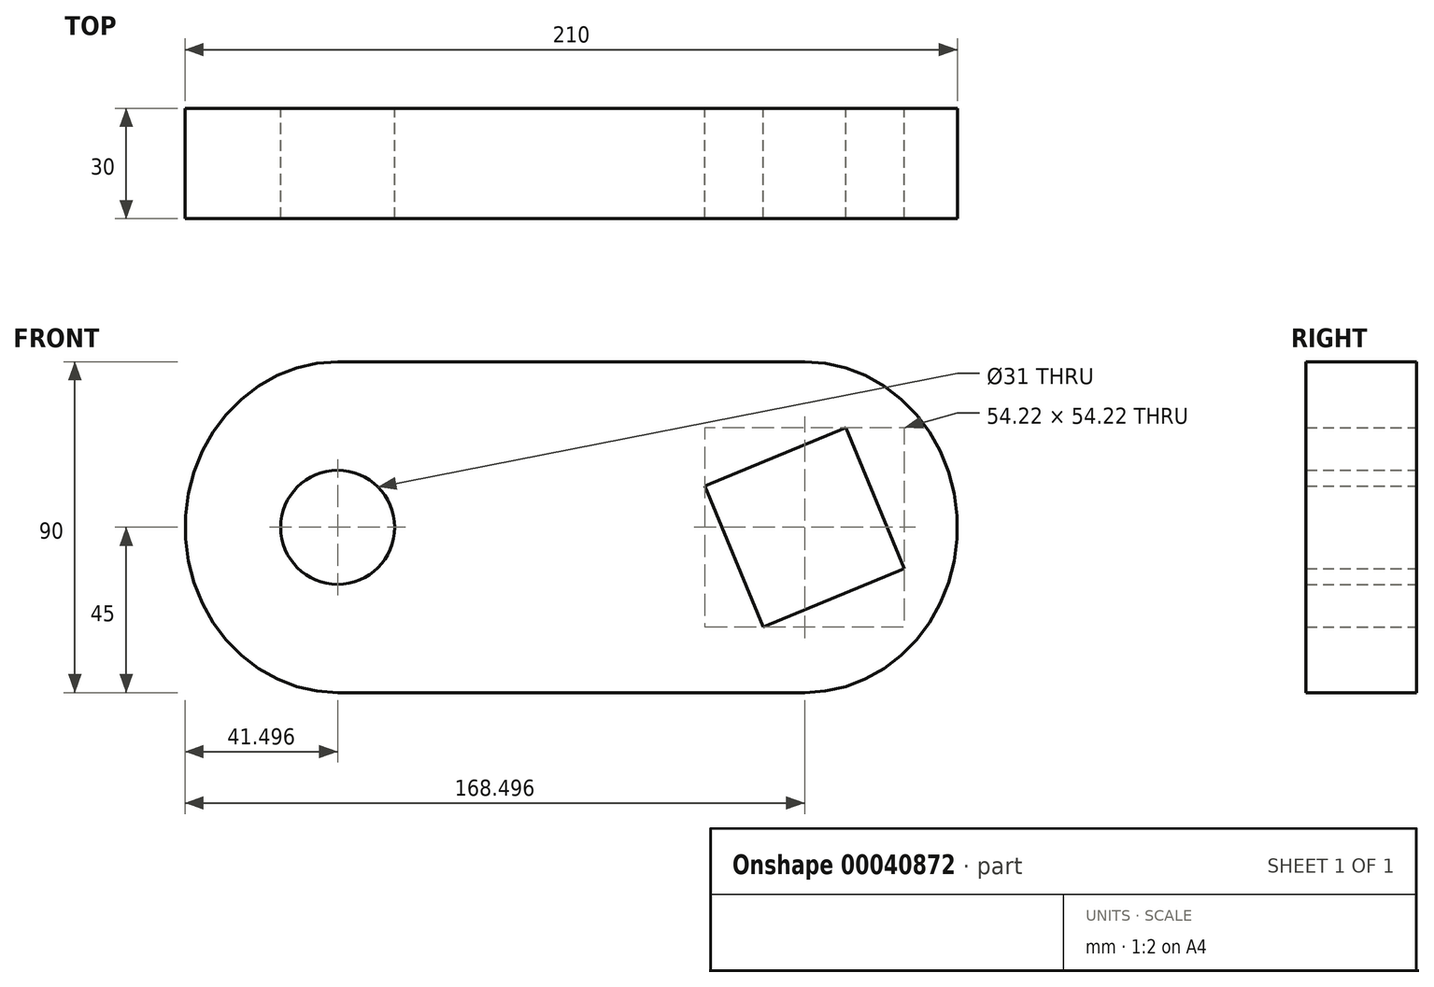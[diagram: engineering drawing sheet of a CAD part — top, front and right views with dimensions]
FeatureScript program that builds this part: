
annotation { "Feature Type Name" : "Feature", "Feature Type Description" : "" }
export const myFeature = defineFeature(function(context is Context, id is Id, definition is map)
    precondition{}
    {
        {
            var Q0;
            Q0=qCreatedBy(makeId("Front.planeOp"),FACE);
            var sketch = newSketch(context, id + "F0", { "sketchPlane" : qUnion([Q0])});
            skCircle(sketch, "E0", {"center": v(-40.02, 0) * mm, "radius": 15.5 * mm});
            skLineSegment(sketch, "E1", {"start": v(-40.02, 0) * mm, "end": v(86.98, 0) * mm});
            skPoint(sketch, "E2.rect.middle", {"position": v(86.98, 0) * mm});
            skEllipticalArc(sketch, "E3", {});
            skEllipticalArc(sketch, "E4", {});
            skLineSegment(sketch, "E5", {"start": v(-40.02, 45) * mm, "end": v(86.98, 45) * mm});
            skLineSegment(sketch, "E6", {"start": v(-40.02, -45) * mm, "end": v(86.98, -45) * mm});
            skLineSegment(sketch, "E7.rect.bottom", {"start": v(98.2, 27.11) * mm, "end": v(59.87, 11.23) * mm});
            skLineSegment(sketch, "E7.rect.top", {"start": v(114.09, -11.23) * mm, "end": v(75.75, -27.11) * mm});
            skLineSegment(sketch, "E7.rect.left", {"start": v(98.2, 27.11) * mm, "end": v(114.09, -11.23) * mm});
            skLineSegment(sketch, "E7.rect.right", {"start": v(59.87, 11.23) * mm, "end": v(75.75, -27.11) * mm});
            const initialGuessF0  = {"E3": [-0.04002362524953623, 0, 0, 1, 0.045, 0.0415, 0, 3.141592653589793], "E4": [0.08697637475046376, 0, 0, 1, 0.045, 0.0415, 3.141592653589793, 0]};
            skSetInitialGuess(sketch, initialGuessF0);
            skSolve(sketch);
        }
        {
            var Q0;
            Q0=makeQuery(id+"F0.imprint","IMPRINT",FACE,{"disambiguationData":[TD([[makeQuery(id+"F0.imprint","IMPRINT",EDGE,{"derivedFrom":sQuery(id+"F0.wireOp",EDGE,"E0")}),-1.0]])]});
            extrude(context, id + "F1", {"entities" : qUnion([Q0]), "depth" : 30 * mm});
        }
    });
